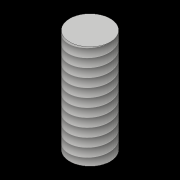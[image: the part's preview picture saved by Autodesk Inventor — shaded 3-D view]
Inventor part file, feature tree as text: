
AUTODESK INVENTOR PART (.ipt)
format: ipt  version: 2017 (Build 210142000, 142)  size: 102,912 bytes
history: native  units: in
note: dims shown in document units (in); Inventor stores cm internally (conversion verified against a paired STEP export)
features: extrude x1, thread x1, sketch x1
ambient origin geometry x8: Origin, YZ Plane, XZ Plane, XY Plane, X Axis, Y Axis, Z Axis, Center Point
bodies: Body1 (feature_tree)
feature tree (3):
  extrude  "Extrusion4"  Depth=0.5in TaperAngle=0.0deg
  thread  "Thread2"  [1 undecoded]
  sketch  "Sketch5"  dims[d11=0.196in d12=0.5in d13=0.0in d14=1.0in d15=0.0in]
note: 1 required parameter value undecoded (feature->parameter linkage not recoverable at this tier; creation-order binding heuristic only, values carry confidence <= 0.55)
